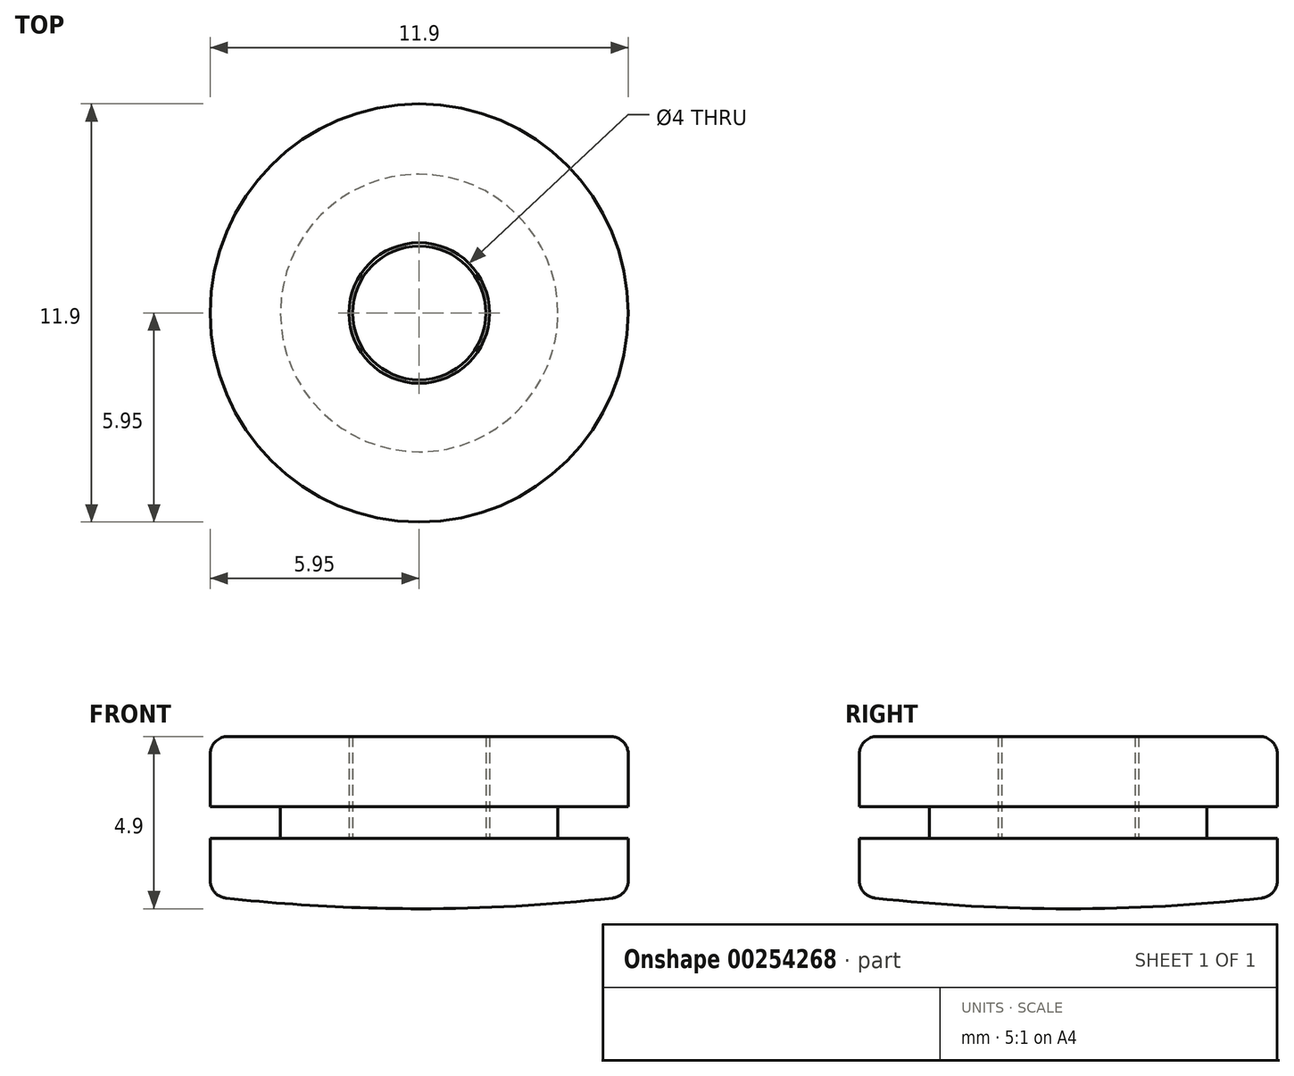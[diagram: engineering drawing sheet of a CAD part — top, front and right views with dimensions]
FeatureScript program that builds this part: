
annotation { "Feature Type Name" : "Feature", "Feature Type Description" : "" }
export const myFeature = defineFeature(function(context is Context, id is Id, definition is map)
    precondition{}
    {
        {
            var Q0;
            Q0=qCreatedBy(makeId("Top.planeOp"),FACE);
            var sketch = newSketch(context, id + "F0", { "sketchPlane" : qUnion([Q0])});
            skCircle(sketch, "E0", {"center": v(0, 0) * mm, "radius": 3.95 * mm});
            skSolve(sketch);
        }
        {
            var Q0;
            Q0=makeQuery(id+"F0.imprint","IMPRINT",FACE,{"disambiguationData":[TD([[makeQuery(id+"F0.imprint","IMPRINT",EDGE,{"derivedFrom":sQuery(id+"F0.wireOp",EDGE,"E0")}),1.0]])]});
            extrude(context, id + "F1", {"entities" : qUnion([Q0]), "depth" : 0.9 * mm});
        }
        {
            var Q0;
            Q0=makeQuery(id+"F1.opExtrude","CAP_FACE",FACE,{"disambiguationData":[OSD([sQuery(id+"F0.wireOp",EDGE,"E0")])],"isStart":false});
            var sketch = newSketch(context, id + "F2", { "sketchPlane" : qUnion([Q0])});
            skCircle(sketch, "E1", {"center": v(0, 0) * mm, "radius": 5.95 * mm});
            skSolve(sketch);
        }
        {
            var Q0;
            Q0=makeQuery(id+"F2.imprint","IMPRINT",FACE,{"disambiguationData":[TD([[makeQuery(id+"F2.imprint","IMPRINT",EDGE,{"derivedFrom":sQuery(id+"F2.wireOp",EDGE,"E1")}),1.0]])]});
            var Q1;
            Q1=makeQuery(id+"F2.imprint","IMPRINT",FACE,{"disambiguationData":[TD([[makeQuery(id+"F2.imprint","IMPRINT",EDGE,{"derivedFrom":makeQuery(id+"F1.opExtrude","CAP_EDGE",EDGE,{"disambiguationData":[OSD([sQuery(id+"F0.wireOp",EDGE,"E0")])],"isStart":false})}),1.0]])]});
            extrude(context, id + "F3", {"entities" : qUnion([Q0, Q1]), "operationType" : NewBodyOperationType.ADD, "depth" : 2 * mm});
        }
        {
            var Q0;
            Q0=makeQuery(id+"F1.opExtrude","CAP_FACE",FACE,{"disambiguationData":[OSD([sQuery(id+"F0.wireOp",EDGE,"E0")])],"isStart":true});
            var sketch = newSketch(context, id + "F4", { "sketchPlane" : qUnion([Q0])});
            skCircle(sketch, "E2", {"center": v(0, 0) * mm, "radius": 2 * mm});
            skSolve(sketch);
        }
        {
            var Q0;
            Q0=makeQuery(id+"F4.imprint","IMPRINT",FACE,{"disambiguationData":[TD([[makeQuery(id+"F4.imprint","IMPRINT",EDGE,{"derivedFrom":sQuery(id+"F4.wireOp",EDGE,"E2")}),1.0]])]});
            extrude(context, id + "F5", {"entities" : qUnion([Q0]), "operationType" : NewBodyOperationType.REMOVE, "endBound" : BoundingType.UP_TO_NEXT, "oppositeDirection" : true, "depth" : 25 * mm});
        }
        {
            var Q0;
            Q0=qCreatedBy(makeId("Front.planeOp"),FACE);
            var sketch = newSketch(context, id + "F6", { "sketchPlane" : qUnion([Q0])});
            skLineSegment(sketch, "E3", {"start": v(0, 0) * mm, "end": v(0, -2) * mm});
            skLineSegment(sketch, "E4", {"start": v(0, 0) * mm, "end": v(-5.95, 0) * mm});
            skLineSegment(sketch, "E5", {"start": v(-5.95, 0) * mm, "end": v(-5.95, -1.64) * mm});
            skLineSegment(sketch, "E6", {"start": v(-5.95, 0.9) * mm, "end": v(-5.95, 2.9) * mm, "construction": true});
            skArc(sketch, "E7", {"start": v(0, -2) * mm, "mid": v(-2.98, -1.91) * mm, "end": v(-5.95, -1.64) * mm});
            skSolve(sketch);
        }
        {
            var Q0;
            Q0=makeQuery(id+"F6.imprint","IMPRINT",FACE,{"disambiguationData":[TD([[makeQuery(id+"F6.imprint","IMPRINT",EDGE,{"derivedFrom":sQuery(id+"F6.wireOp",EDGE,"E3")}),-1.0]])]});
            var Q1;
            Q1=sQuery(id+"F6.wireOp",EDGE,"E3");
            revolve(context, id + "F7", {"entities" : qUnion([Q0]), "axis" : qUnion([Q1]), "revolveType" : RevolveType.FULL});
        }
        {
            var Q0;
            Q0=makeQuery(id+"F7.opRevolve","SWEPT_FACE",FACE,{"disambiguationData":[OSD([sQuery(id+"F6.wireOp",EDGE,"E4")])]});
            var sketch = newSketch(context, id + "F8", { "sketchPlane" : qUnion([Q0])});
            skCircle(sketch, "E8.0", {"center": v(0, 0) * mm, "radius": 2 * mm, "construction": true});
            skCircle(sketch, "E9.0", {"center": v(0, 0) * mm, "radius": 1.9 * mm});
            skSolve(sketch);
        }
        {
            var Q0;
            Q0=makeQuery(id+"F8.imprint","IMPRINT",FACE,{"disambiguationData":[TD([[makeQuery(id+"F8.imprint","IMPRINT",EDGE,{"derivedFrom":sQuery(id+"F8.wireOp",EDGE,"E9.0")}),1.0]])]});
            var Q1;
            Q1=makeQuery(id+"F3.opExtrude","CAP_FACE",FACE,{"disambiguationData":[OSD([sQuery(id+"F2.wireOp",EDGE,"E1")])],"isStart":false});
            extrude(context, id + "F9", {"entities" : qUnion([Q0]), "operationType" : NewBodyOperationType.ADD, "endBound" : BoundingType.UP_TO_SURFACE, "endBoundEntityFace" : qUnion([Q1]), "depth" : 25 * mm});
        }
        {
            var Q0;
            Q0=makeQuery(id+"F3.opExtrude","CAP_EDGE",EDGE,{"disambiguationData":[OSD([sQuery(id+"F2.wireOp",EDGE,"E1")])],"isStart":false});
            var Q1;
            Q1=makeQuery(id+"F7.opRevolve","SWEPT_EDGE",EDGE,{"disambiguationData":[OSD([sQuery(id+"F6.wireOp",EDGE,"E5"),sQuery(id+"F6.wireOp",EDGE,"E7")])]});
            fillet(context, id + "F10", {"entities" : qUnion([Q0, Q1]), "radius" : .5 * mm, "tangentPropagation" : true, "allowEdgeOverflow" : false});
        }
    });
